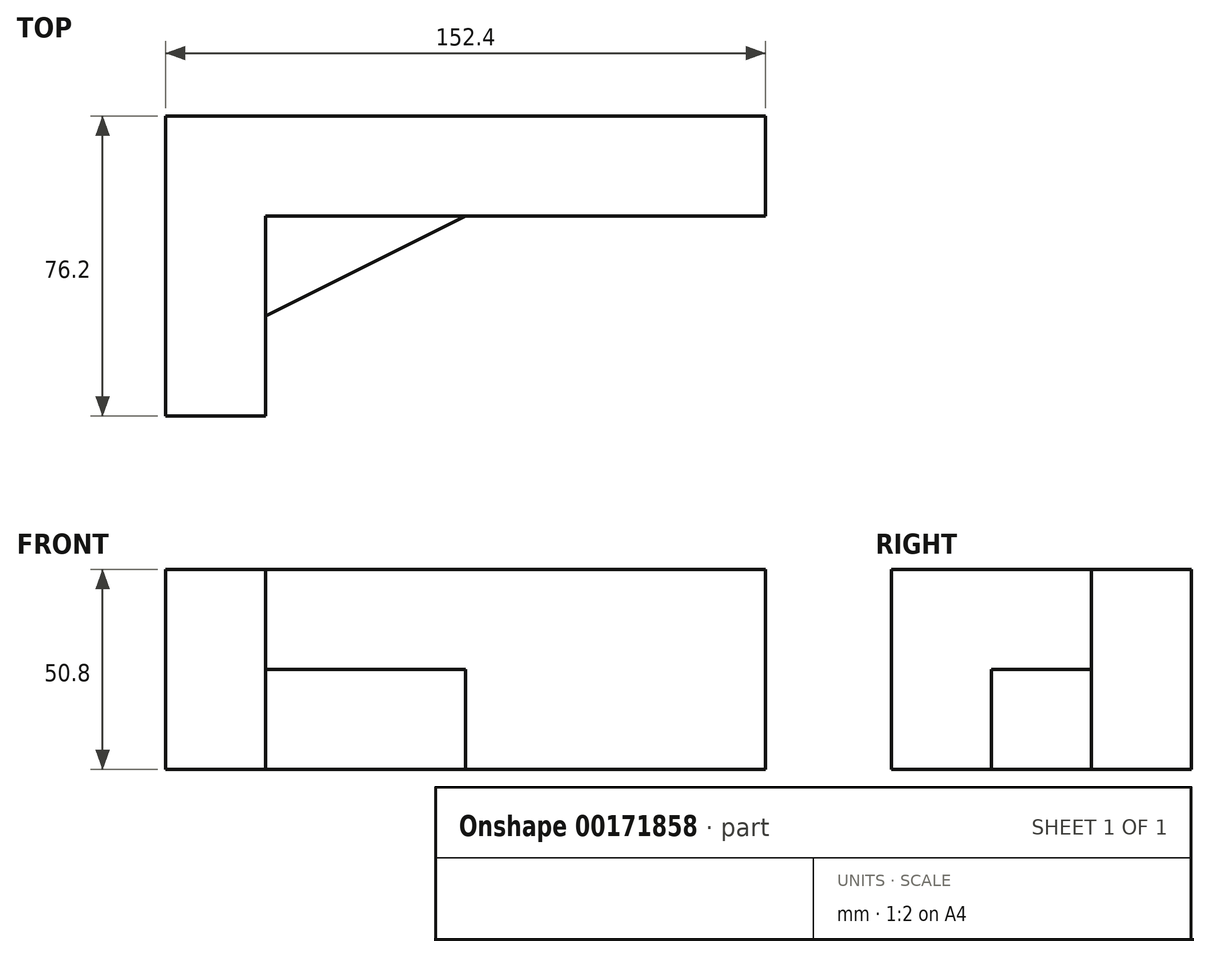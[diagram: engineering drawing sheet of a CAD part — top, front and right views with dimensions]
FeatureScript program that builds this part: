
annotation { "Feature Type Name" : "Feature", "Feature Type Description" : "" }
export const myFeature = defineFeature(function(context is Context, id is Id, definition is map)
    precondition{}
    {
        {
            var Q0;
            Q0=qCreatedBy(makeId("Top.planeOp"),FACE);
            var sketch = newSketch(context, id + "F0", { "sketchPlane" : qUnion([Q0])});
            skLineSegment(sketch, "E0", {"start": v(-62.86, 81.54) * mm, "end": v(89.54, 81.54) * mm});
            skLineSegment(sketch, "E1", {"start": v(-62.86, 81.54) * mm, "end": v(-62.86, 5.34) * mm});
            skLineSegment(sketch, "E2", {"start": v(89.54, 81.54) * mm, "end": v(89.54, 56.14) * mm});
            skLineSegment(sketch, "E3", {"start": v(-62.86, 5.34) * mm, "end": v(-37.46, 5.34) * mm});
            skLineSegment(sketch, "E4", {"start": v(89.54, 56.14) * mm, "end": v(-37.46, 56.14) * mm});
            skLineSegment(sketch, "E5", {"start": v(-37.46, 56.14) * mm, "end": v(-37.46, 5.34) * mm});
            skLineSegment(sketch, "E6", {"start": v(-37.46, 5.34) * mm, "end": v(-37.46, 30.74) * mm});
            skLineSegment(sketch, "E7", {"start": v(-37.46, 56.14) * mm, "end": v(13.34, 56.14) * mm});
            skLineSegment(sketch, "E8", {"start": v(-37.46, 30.74) * mm, "end": v(13.34, 56.14) * mm});
            skSolve(sketch);
        }
        {
            var Q0;
            Q0=makeQuery(id+"F0.imprint","IMPRINT",FACE,{"disambiguationData":[TD([[makeQuery(id+"F0.imprint","IMPRINT",EDGE,{"derivedFrom":sQuery(id+"F0.wireOp",EDGE,"E0")}),-1.0]])]});
            extrude(context, id + "F1", {"entities" : qUnion([Q0]), "depth" : 50.8 * mm});
        }
        {
            var Q0;
            Q0=makeQuery(id+"F0.imprint","IMPRINT",FACE,{"disambiguationData":[TD([[makeQuery(id+"F0.imprint","IMPRINT",EDGE,{"derivedFrom":sQuery(id+"F0.wireOp",EDGE,"E5")}),1.0]])]});
            extrude(context, id + "F2", {"entities" : qUnion([Q0]), "operationType" : NewBodyOperationType.ADD, "depth" : 25.4 * mm});
        }
    });
